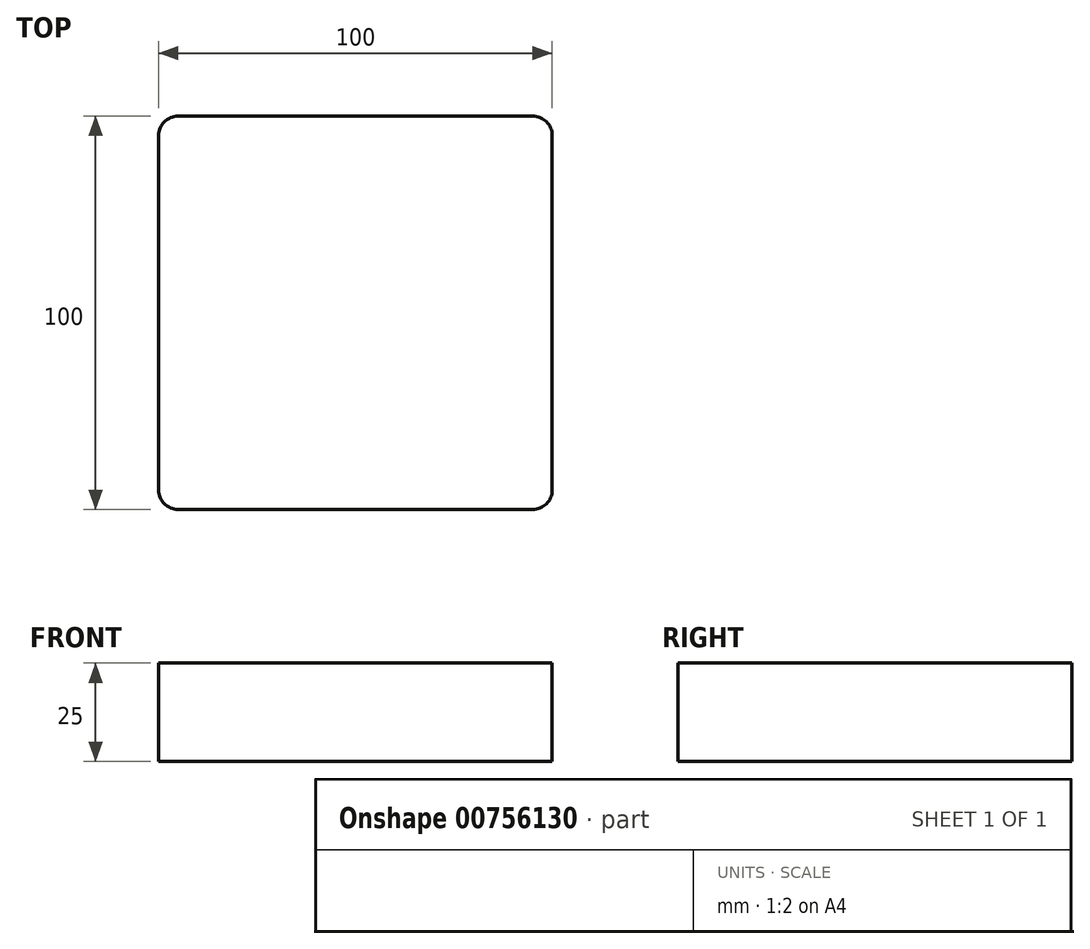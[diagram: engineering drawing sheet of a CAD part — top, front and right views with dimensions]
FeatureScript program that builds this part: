
annotation { "Feature Type Name" : "Feature", "Feature Type Description" : "" }
export const myFeature = defineFeature(function(context is Context, id is Id, definition is map)
    precondition{}
    {
        {
            var Q0;
            Q0=qCreatedBy(makeId("Top.planeOp"),FACE);
            var sketch = newSketch(context, id + "F0", { "sketchPlane" : qUnion([Q0])});
            skLineSegment(sketch, "E0.bottom", {"start": v(-50, -52.07) * mm, "end": v(50, -52.07) * mm});
            skLineSegment(sketch, "E0.top", {"start": v(-50, 47.93) * mm, "end": v(50, 47.93) * mm});
            skLineSegment(sketch, "E0.left", {"start": v(-50, -52.07) * mm, "end": v(-50, 47.93) * mm});
            skLineSegment(sketch, "E0.right", {"start": v(50, -52.07) * mm, "end": v(50, 47.93) * mm});
            skPoint(sketch, "E0.middle", {"position": v(0, -2.07) * mm});
            skSolve(sketch);
        }
        {
            var Q0;
            Q0=makeQuery(id+"F0.imprint","IMPRINT",FACE,{"disambiguationData":[TD([[makeQuery(id+"F0.imprint","IMPRINT",EDGE,{"derivedFrom":sQuery(id+"F0.wireOp",EDGE,"E0.bottom")}),1.0]])]});
            extrude(context, id + "F1", {"entities" : qUnion([Q0]), "depth" : 25 * mm, "offsetDistance" : 25 * mm});
        }
        {
            var Q0;
            Q0=makeQuery(id+"F1.opExtrude","SWEPT_EDGE",EDGE,{"disambiguationData":[OSD([sQuery(id+"F0.wireOp",EDGE,"E0.bottom"),sQuery(id+"F0.wireOp",EDGE,"E0.left")])]});
            var Q1;
            Q1=makeQuery(id+"F1.opExtrude","SWEPT_EDGE",EDGE,{"disambiguationData":[OSD([sQuery(id+"F0.wireOp",EDGE,"E0.bottom"),sQuery(id+"F0.wireOp",EDGE,"E0.right")])]});
            var Q2;
            Q2=makeQuery(id+"F1.opExtrude","SWEPT_EDGE",EDGE,{"disambiguationData":[OSD([sQuery(id+"F0.wireOp",EDGE,"E0.top"),sQuery(id+"F0.wireOp",EDGE,"E0.right")])]});
            var Q3;
            Q3=makeQuery(id+"F1.opExtrude","SWEPT_EDGE",EDGE,{"disambiguationData":[OSD([sQuery(id+"F0.wireOp",EDGE,"E0.top"),sQuery(id+"F0.wireOp",EDGE,"E0.left")])]});
            fillet(context, id + "F2", {"entities" : qUnion([Q0, Q1, Q2, Q3]), "tangentPropagation" : true, "radius" : 5 * mm, "defaultsChanged" : false, "vertexSettings" : [], "allowEdgeOverflow" : false});
        }
    });
